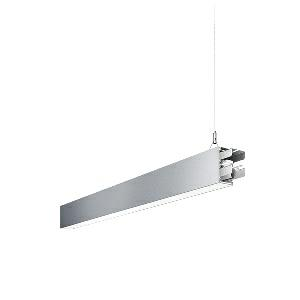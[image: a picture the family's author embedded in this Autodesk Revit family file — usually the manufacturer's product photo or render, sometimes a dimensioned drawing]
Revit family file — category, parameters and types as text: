
# Revit family: dotoo_line_-_dlp_1500_840_d_mid_00805823_ce63
name_source: partatom
category: Lighting Fixtures
units: mm (PartAtom-declared; Revit-internal decimal feet)

## family parameters
Cut with Voids When Loaded = No
Host = Face
Light Source = No
Part Type = Normal
Room Calculation Point = No
Round Connector Dimension = Use Diameter
Shared = No

## types (1)
- DOTOO.line - DLP 1500/840/D MID (1 x LED, 1350 lm, 4000K)
    Apparent Load = 13 VA
    Approval mark = CE
    CIE Flux Codes = 67 91 98 100 100
    Color Rendering = 80-89
    Color Temperature = 4000K
    Control Gear = Electronic ballast
    Default Elevation = 1800 mm
    Description = DLP 1500/840/D|Suspended luminaire|light source: LED|connected load: 220-240 V, 50/60 Hz|Power consumption: approx. 13 W|standby: approx. 0,20|luminous flux: 1350 lm|luminous efficacy: 103 lm/W|light distribution: Direct|direct ratio: approx. 100 %|colour temperature: Cold white, ca. 4000 K|color rendering index (CRI): >= 80|chromaticity tolerance:  3 SDCM|System of protection: IP 40|technology: Continuously dimmable|luminaire body|material: Sectional aluminium|colour: Silver|lamp cover: Acrylic (PMMA), Clear|mains lead: 1,0 m With free stranded wires|Fastening: Steel cable 0.3 - 0.7 m|glare control: Prism aperture|luminance(L65): <= 3000 cd/m|unified glare rating(4H 8H): <=  19|special features: DALI Load 1x, TouchDIM - dimming via standard switch, Through-wired, up to 18 m on one mains connection, Flicker-free, Suitable as emergency lighting, Mechanical and electrical connection of the individual modules without tools|
    Frequency = 50 Hz
    Height = 110 mm
    Lamp = 1 x LED
    Lamp Light Flux = 1350 lm
    Lamp count = 1
    Length = 1122 mm
    Luminous efficacy = 104 lm/W
    Manufacturer = Waldmann
    ModVariant = No
    Model = 00805823
    Mounting Place = Ceiling
    Mounting Type = Pendant
    Number of Poles = 1
    OnlyDefault = Yes
    Power Factor = 1
    Product Name = DOTOO.line - DLP 1500/840/D MID
    Product group = Suspended luminaire
    ProductGroupID = 9
    Protection Class = Protection class I
    Protection Degree = IP 40
    RLX_Detail_Level = 1
    RLX_Emergency_Light_Flux = 0 lm
    RLX_Emergency_Type = 0
    RLX_Emergency_Type_DB = No
    RlxData = <blob elided: 21081 chars, md5=64f6e520>
    Socket = socket
    Standby Power = 0 W
    System Light Flux = 1350 lm
    System Power = 13 W
    Type Comments = Product without accessories
    Type Image = 113305000-00692579.jpg
    URL = http://relux.com
    VarID = ---
    Voltage = 230 V
    Voltage Range = 220-240 V
    Weight = 0.00 kg
    Width = 60 mm  [stored 0.19685 ft]

note: [stored X ft] marks values corroborated as IEEE doubles in the binary element streams (Revit-internal decimal feet)

## geometry (parser evidence)
native form markers: Blend x4, Sweep x10
no freeform markers — native parametric forms only
